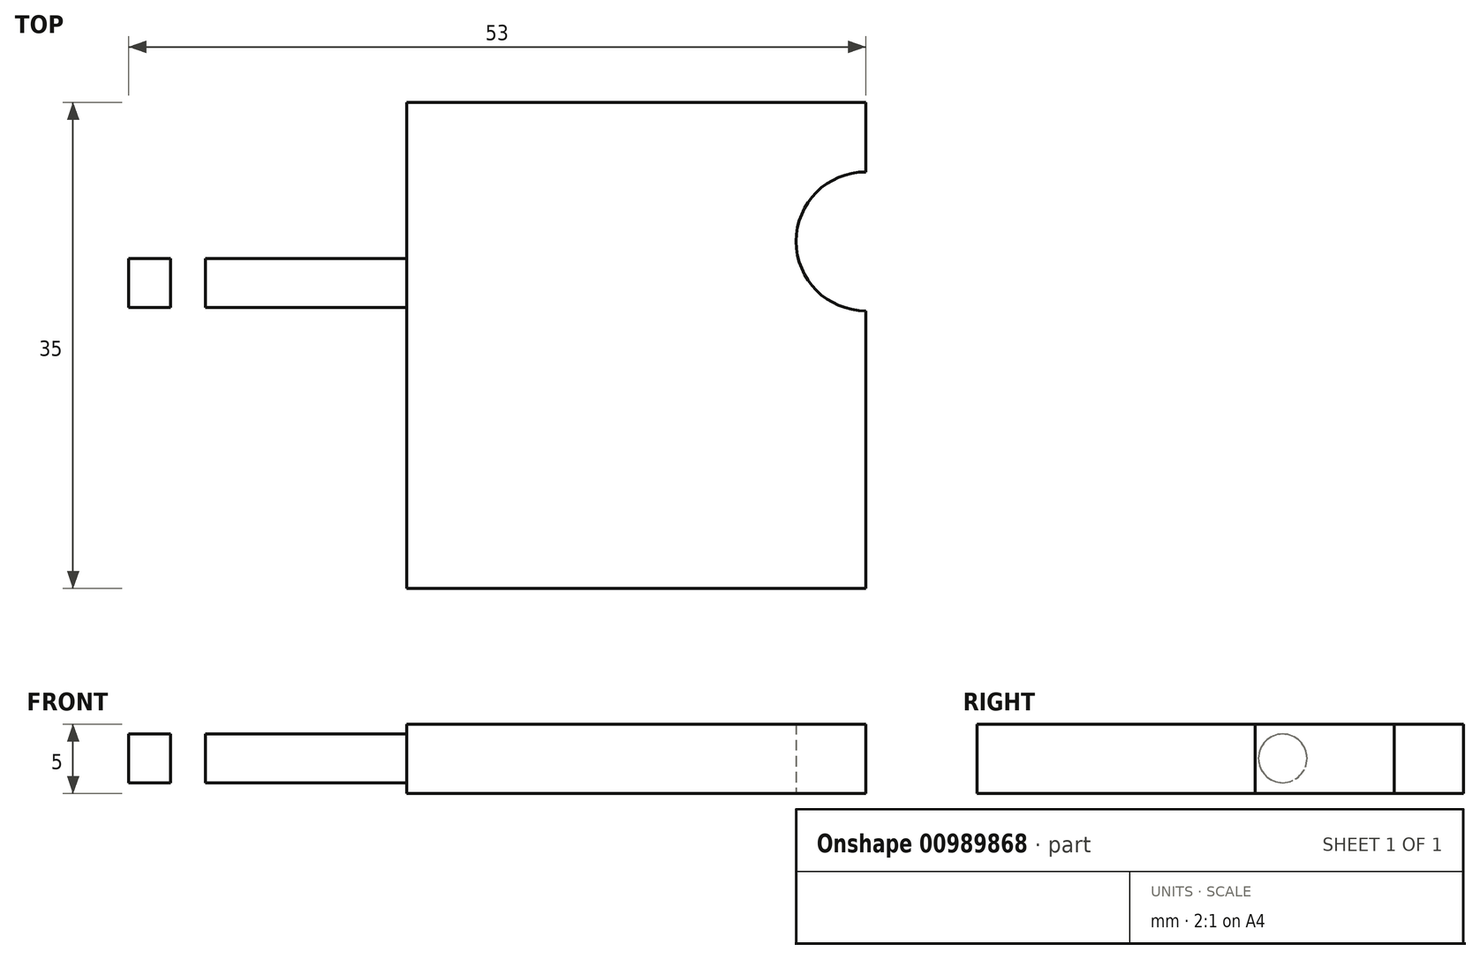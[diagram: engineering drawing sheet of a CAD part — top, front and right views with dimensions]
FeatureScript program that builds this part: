
annotation { "Feature Type Name" : "Feature", "Feature Type Description" : "" }
export const myFeature = defineFeature(function(context is Context, id is Id, definition is map)
    precondition{}
    {
        {
            var Q0;
            Q0=qCreatedBy(makeId("Top.planeOp"),FACE);
            var sketch = newSketch(context, id + "F0", { "sketchPlane" : qUnion([Q0])});
            skLineSegment(sketch, "E0.bottom", {"start": v(-53, 35) * mm, "end": v(0, 35) * mm});
            skLineSegment(sketch, "E0.left", {"start": v(-53, 35) * mm, "end": v(-53, 0) * mm});
            skPoint(sketch, "E0.middle", {"position": v(0, 0) * mm});
            skLineSegment(sketch, "E1", {"start": v(-53, 25) * mm, "end": v(0, 25) * mm});
            skLineSegment(sketch, "E2", {"start": v(-50, 35) * mm, "end": v(-50, 0) * mm});
            skLineSegment(sketch, "E3.bottom", {"start": v(-50, 25) * mm, "end": v(-47.5, 25) * mm});
            skLineSegment(sketch, "E3.top", {"start": v(-50, 19) * mm, "end": v(-47.5, 19) * mm});
            skLineSegment(sketch, "E3.left", {"start": v(-50, 25) * mm, "end": v(-50, 19) * mm});
            skLineSegment(sketch, "E3.right", {"start": v(-47.5, 25) * mm, "end": v(-47.5, 19) * mm});
            skArc(sketch, "E4", {"start": v(0, 30) * mm, "mid": v(-5, 25) * mm, "end": v(0, 20) * mm});
            skLineSegment(sketch, "E5", {"start": v(-50, 22) * mm, "end": v(-47.5, 22) * mm});
            skLineSegment(sketch, "E6", {"start": v(-50, 22) * mm, "end": v(-53, 22) * mm});
            skLineSegment(sketch, "E7", {"start": v(0, 35) * mm, "end": v(0, 0) * mm});
            skLineSegment(sketch, "E8.trimOffspring", {"start": v(0, 25) * mm, "end": v(-53, 25) * mm});
            skPoint(sketch, "E9.MirrorCS.end.orphan", {"position": v(47.5, 19) * mm});
            skPoint(sketch, "E10.MirrorCS.end.orphan", {"position": v(47.5, -19) * mm});
            skPoint(sketch, "E11.orphan", {"position": v(53, 35) * mm});
            skPoint(sketch, "E12.orphan", {"position": v(53, 25) * mm});
            skPoint(sketch, "E13.trimOffspring.end.orphan", {"position": v(50, 19) * mm});
            skPoint(sketch, "E14.MirrorCS.start.orphan", {"position": v(50, 35) * mm});
            skPoint(sketch, "E15.orphan", {"position": v(50, -19) * mm});
            skPoint(sketch, "E0.right.start.orphan", {"position": v(53, -25) * mm});
            skPoint(sketch, "E16.MirrorCS.start.orphan", {"position": v(50, -35) * mm});
            skLineSegment(sketch, "E17", {"start": v(-53, 0) * mm, "end": v(0, 0) * mm});
            skPoint(sketch, "E18.trimOffspring.start.orphan", {"position": v(47.5, 25) * mm});
            skPoint(sketch, "E19.trimOffspring.end.orphan", {"position": v(53, -35) * mm});
            skPoint(sketch, "E20.MirrorCS.end.orphan", {"position": v(47.5, -25) * mm});
            skPoint(sketch, "E21.orphan", {"position": v(0, -35) * mm});
            skLineSegment(sketch, "E22.trimOffspring", {"start": v(-50, 0) * mm, "end": v(-50, 35) * mm});
            skPoint(sketch, "E23.MirrorCS.end.orphan", {"position": v(-47.5, -19) * mm});
            skPoint(sketch, "E24.MirrorCS.start.orphan", {"position": v(-50, -19) * mm});
            skPoint(sketch, "E0.top.end.orphan", {"position": v(-50, -35) * mm});
            skPoint(sketch, "E0.top.start.orphan", {"position": v(-53, -35) * mm});
            skPoint(sketch, "E25.trimOffspring.end.orphan", {"position": v(-53, -25) * mm});
            skPoint(sketch, "E25.trimOffspring.start.orphan", {"position": v(-47.5, -25) * mm});
            skSolve(sketch);
        }
        {
            var Q0;
            {var subQ1=sQuery(id+"F0.wireOp",EDGE,"E3.top");Q0=makeQuery(id+"F0.imprint","IMPRINT",FACE,{"disambiguationData":[TD([[makeQuery(id+"F0.imprint","IMPRINT",EDGE,{"derivedFrom":subQ1}),-1.0]])]});}
            var Q1;
            {var subQ2=sQuery(id+"F0.wireOp",EDGE,"b1ba5556-9fe2-4869-8879-02e2251251430.MirrorCS");var subQ7=sQuery(id+"F0.wireOp",EDGE,"E0.top");var subQ8=makeQuery(id+"F0.imprint","INTERSECT",VERTEX,{"derivedFrom":[subQ7,subQ2]});Q1=makeQuery(id+"F0.imprint","IMPRINT",FACE,{"disambiguationData":[TD([[makeQuery(id+"F0.imprint","IMPRINT",EDGE,{"disambiguationData":[TD([[subQ8,-1.0]])],"derivedFrom":subQ7}),1.0]])]});}
            var Q2;
            {var subQ7=sQuery(id+"F0.wireOp",EDGE,"E6");Q2=makeQuery(id+"F0.imprint","IMPRINT",FACE,{"disambiguationData":[TD([[makeQuery(id+"F0.imprint","IMPRINT",EDGE,{"derivedFrom":subQ7}),1.0]])]});}
            var Q3;
            {var subQ0=sQuery(id+"F0.wireOp",EDGE,"E0.left");var subQ1=sQuery(id+"F0.wireOp",EDGE,"E0.top");var subQ2=makeQuery(id+"F0.imprint","INTERSECT",VERTEX,{"derivedFrom":[subQ1,subQ0]});Q3=makeQuery(id+"F0.imprint","IMPRINT",FACE,{"disambiguationData":[TD([[makeQuery(id+"F0.imprint","IMPRINT",EDGE,{"disambiguationData":[TD([[subQ2,-1.0]])],"derivedFrom":subQ1}),1.0]])]});}
            var Q4;
            {var subQ0=sQuery(id+"F0.wireOp",EDGE,"E0.left");var subQ1=sQuery(id+"F0.wireOp",EDGE,"E0.bottom");var subQ2=makeQuery(id+"F0.imprint","INTERSECT",VERTEX,{"derivedFrom":[subQ1,subQ0]});Q4=makeQuery(id+"F0.imprint","IMPRINT",FACE,{"disambiguationData":[TD([[makeQuery(id+"F0.imprint","IMPRINT",EDGE,{"disambiguationData":[TD([[subQ2,-1.0]])],"derivedFrom":subQ1}),-1.0]])]});}
            var Q5;
            {var subQ3=sQuery(id+"F0.wireOp",EDGE,"E6");Q5=makeQuery(id+"F0.imprint","IMPRINT",FACE,{"disambiguationData":[TD([[makeQuery(id+"F0.imprint","IMPRINT",EDGE,{"derivedFrom":subQ3}),-1.0]])]});}
            var Q6;
            {var subQ5=sQuery(id+"F0.wireOp",EDGE,"E0.bottom");var subQ10=sQuery(id+"F0.wireOp",EDGE,"b1ba5556-9fe2-4869-8879-02e2251251430.MirrorCS");var subQ11=makeQuery(id+"F0.imprint","INTERSECT",VERTEX,{"derivedFrom":[subQ5,subQ10]});Q6=makeQuery(id+"F0.imprint","IMPRINT",FACE,{"disambiguationData":[TD([[makeQuery(id+"F0.imprint","IMPRINT",EDGE,{"disambiguationData":[TD([[subQ11,-1.0]])],"derivedFrom":subQ5}),-1.0]])]});}
            var Q7;
            {var subQ0=sQuery(id+"F0.wireOp",EDGE,"E0.right");var subQ1=sQuery(id+"F0.wireOp",EDGE,"E0.bottom");var subQ2=makeQuery(id+"F0.imprint","INTERSECT",VERTEX,{"derivedFrom":[subQ1,subQ0]});Q7=makeQuery(id+"F0.imprint","IMPRINT",FACE,{"disambiguationData":[TD([[makeQuery(id+"F0.imprint","IMPRINT",EDGE,{"disambiguationData":[TD([[subQ2,1.0]])],"derivedFrom":subQ1}),-1.0]])]});}
            var Q8;
            {var subQ1=sQuery(id+"F0.wireOp",EDGE,"E0.right");var subQ5=sQuery(id+"F0.wireOp",EDGE,"ced93293-8bf0-40b2-a98f-60756c3920860.MirrorCS");var subQ6=makeQuery(id+"F0.imprint","INTERSECT",VERTEX,{"derivedFrom":[subQ1,subQ5]});Q8=makeQuery(id+"F0.imprint","IMPRINT",FACE,{"disambiguationData":[TD([[makeQuery(id+"F0.imprint","IMPRINT",EDGE,{"disambiguationData":[TD([[subQ6,-1.0]])],"derivedFrom":subQ1}),-1.0]])]});}
            var Q9;
            {var subQ0=sQuery(id+"F0.wireOp",EDGE,"E0.right");var subQ1=sQuery(id+"F0.wireOp",EDGE,"E0.top");var subQ2=makeQuery(id+"F0.imprint","INTERSECT",VERTEX,{"derivedFrom":[subQ1,subQ0]});Q9=makeQuery(id+"F0.imprint","IMPRINT",FACE,{"disambiguationData":[TD([[makeQuery(id+"F0.imprint","IMPRINT",EDGE,{"disambiguationData":[TD([[subQ2,1.0]])],"derivedFrom":subQ1}),1.0]])]});}
            var Q10;
            {var subQ4=sQuery(id+"F0.wireOp",EDGE,"E7");var subQ5=sQuery(id+"F0.wireOp",EDGE,"E0.bottom");var subQ6=makeQuery(id+"F0.imprint","INTERSECT",VERTEX,{"derivedFrom":[subQ5,subQ4]});Q10=makeQuery(id+"F0.imprint","IMPRINT",FACE,{"disambiguationData":[TD([[makeQuery(id+"F0.imprint","IMPRINT",EDGE,{"disambiguationData":[TD([[subQ6,1.0]])],"derivedFrom":subQ5}),-1.0]])]});}
            extrude(context, id + "F1", {"entities" : qUnion([Q0, Q1, Q2, Q3, Q4, Q5, Q6, Q7, Q8, Q9, Q10]), "depth" : 5 * mm, "offsetDistance" : 25 * mm});
        }
        {
            var Q0;
            Q0=makeQuery(id+"F1.opExtrude","SWEPT_FACE",FACE,{"disambiguationData":[OSD([sQuery(id+"F0.wireOp",EDGE,"E0.left")])]});
            var sketch = newSketch(context, id + "F2", { "sketchPlane" : qUnion([Q0])});
            skLineSegment(sketch, "E26.bottom", {"start": v(35, -5) * mm, "end": v(-35, -5) * mm});
            skLineSegment(sketch, "E26.top", {"start": v(35, 5) * mm, "end": v(-35, 5) * mm});
            skLineSegment(sketch, "E26.left", {"start": v(35, -5) * mm, "end": v(35, 5) * mm});
            skLineSegment(sketch, "E26.right", {"start": v(-35, -5) * mm, "end": v(-35, 5) * mm});
            skPoint(sketch, "E26.middle", {"position": v(0, 0) * mm});
            skLineSegment(sketch, "E27", {"start": v(-35, 0) * mm, "end": v(35, 0) * mm});
            skPoint(sketch, "E28", {"position": v(25, 0) * mm});
            skPoint(sketch, "E29", {"position": v(22, 0) * mm});
            skLineSegment(sketch, "E30", {"start": v(22, 0) * mm, "end": v(22, 5) * mm});
            skLineSegment(sketch, "E31", {"start": v(22, 2.53) * mm, "end": v(35, 2.5) * mm});
            skPoint(sketch, "E31.endSnap0", {"position": v(22, 2.5) * mm});
            skCircle(sketch, "E32", {"center": v(22, 2.53) * mm, "radius": 1.75 * mm});
            skCircle(sketch, "E33.MirrorC", {"center": v(-22, 2.53) * mm, "radius": 1.75 * mm});
            skSolve(sketch);
        }
        {
            var Q0;
            Q0=makeQuery(id+"F2.imprint","IMPRINT",FACE,{"disambiguationData":[TD([[makeQuery(id+"F2.imprint","IMPRINT",EDGE,{"derivedFrom":sQuery(id+"F2.wireOp",EDGE,"E33.MirrorC")}),-1.0]])]});
            extrude(context, id + "F3", {"entities" : qUnion([Q0]), "operationType" : NewBodyOperationType.REMOVE, "depth" : -20 * mm, "offsetDistance" : 25 * mm});
        }
        {
            var Q0;
            {var subQ0=sQuery(id+"F2.wireOp",EDGE,"E30");var subQ1=makeQuery(id+"F2.imprint","INTERSECT",VERTEX,{"derivedFrom":[subQ0,sQuery(id+"F2.wireOp",EDGE,"E31")]});Q0=makeQuery(id+"F2.imprint","IMPRINT",FACE,{"disambiguationData":[TD([[makeQuery(id+"F2.imprint","IMPRINT",EDGE,{"disambiguationData":[TD([[subQ1,1.0]])],"derivedFrom":subQ0}),1.0]])]});}
            var Q1;
            {var subQ0=sQuery(id+"F2.wireOp",EDGE,"E31");var subQ1=sQuery(id+"F2.wireOp",EDGE,"E30");var subQ2=makeQuery(id+"F2.imprint","INTERSECT",VERTEX,{"derivedFrom":[subQ1,subQ0]});Q1=makeQuery(id+"F2.imprint","IMPRINT",FACE,{"disambiguationData":[TD([[makeQuery(id+"F2.imprint","IMPRINT",EDGE,{"disambiguationData":[TD([[subQ2,1.0]])],"derivedFrom":subQ1}),-1.0]])]});}
            var Q2;
            {var subQ0=sQuery(id+"F2.wireOp",EDGE,"E31");var subQ1=sQuery(id+"F2.wireOp",EDGE,"E30");var subQ2=makeQuery(id+"F2.imprint","INTERSECT",VERTEX,{"derivedFrom":[subQ1,subQ0]});Q2=makeQuery(id+"F2.imprint","IMPRINT",FACE,{"disambiguationData":[TD([[makeQuery(id+"F2.imprint","IMPRINT",EDGE,{"disambiguationData":[TD([[subQ2,-1.0]])],"derivedFrom":subQ1}),-1.0]])]});}
            extrude(context, id + "F4", {"entities" : qUnion([Q0, Q1, Q2]), "operationType" : NewBodyOperationType.REMOVE, "oppositeDirection" : true, "depth" : 20 * mm, "offsetDistance" : 25 * mm});
        }
    });
